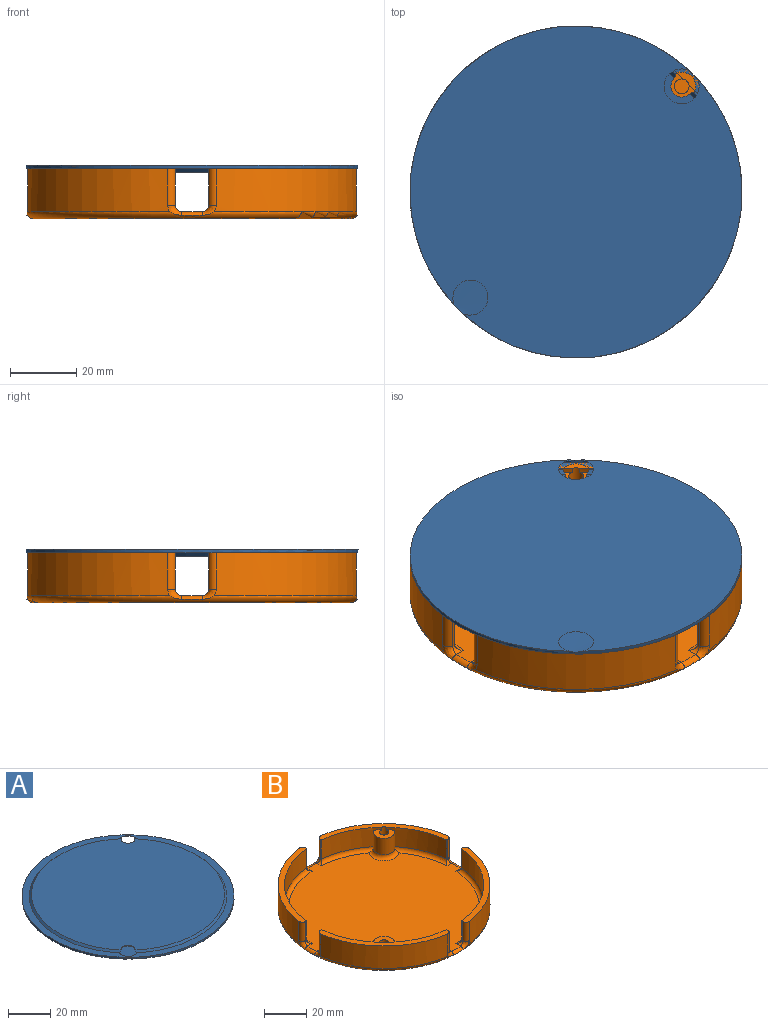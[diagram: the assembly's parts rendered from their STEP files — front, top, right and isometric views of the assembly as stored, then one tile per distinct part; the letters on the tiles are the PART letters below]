
ASSEMBLY  parts=2 mates=1
PART A: 8 faces, bbox 100x100x2 mm
  f0: cylinder r=50mm len=100mm, axis (0,0,-1), area 313mm2, adj f1,f2,f4,f5
  f1: plane 100x100mm, normal (0,0,1), area 1028.4mm2, adj f0,f4,f5,f6,f7
  f2: plane 100x100mm, normal (0,0,-1), area 7681.9mm2, adj f0,f4,f5
  f3: plane 91x91mm, normal (0,0,1), area 6464.7mm2, adj f4,f5,f6,f7
  f4: cone r=5.25mm half-angle=45deg, axis (0,0,-1), area 60.4mm2, adj f0,f1,f2,f3,f6,f7
  f5: cone r=5.25mm half-angle=45deg, axis (0,0,-1), area 60.4mm2, adj f0,f1,f2,f3,f6,f7
  f6: cone r=45.5mm half-angle=45deg, axis (0,0,-1), area 194.1mm2, adj f1,f3,f4,f5
  f7: cone r=45.5mm half-angle=45deg, axis (0,0,-1), area 194.1mm2, adj f1,f3,f4,f5
PART B: 69 faces, bbox 108.2x108.2x15 mm
  f0: cylinder r=5mm len=9.56mm, axis (0,0,-1), area 183.5mm2, adj f14,f16,f30,f68
  f1: cylinder r=5mm len=9.56mm, axis (0,0,-1), area 183.5mm2, adj f25,f27,f36,f67
  f2: cylinder r=50mm len=42.81mm, axis (0,0,-1), area 831.9mm2, adj f17,f42,f43,f55,f56,f64
  f3: cylinder r=50mm len=42.81mm, axis (0,0,-1), area 831.9mm2, adj f22,f46,f47,f58,f59,f64
  f4: cylinder r=50mm len=42.81mm, axis (0,0,-1), area 831.9mm2, adj f28,f50,f61,f64,f65,f66
  f5: plane 96x96mm, normal (0,0,1), area 6284.9mm2, adj f30,f31,f32,f33,f34,f35,f36,f37
  f6: cylinder r=50mm len=42.81mm, axis (0,0,-1), area 831.9mm2, adj f11,f38,f39,f52,f53,f64
  f7: plane 96x96mm, normal (0,0,-1), area 7238.2mm2, adj f64
  f8: plane 11x0.75mm, normal (1,0,0), area 8.3mm2, adj f10,f11,f37,f38
  f9: plane 11x0.75mm, normal (0,-1,0), area 8.3mm2, adj f10,f11,f39,f40
  f10: cylinder r=47mm len=41.73mm, axis (0,0,-1), area 701.9mm2, adj f8,f9,f11,f31
  f11: plane 44.49x44.49mm, normal (0,0,1), area 196.2mm2, adj f6,f8,f9,f10,f38,f39
  f12: plane 11x0.75mm, normal (0,1,0), area 8.3mm2, adj f16,f17,f41,f42
  f13: plane 11x0.75mm, normal (1,0,0), area 8.3mm2, adj f14,f17,f43,f44
  f14: cylinder r=47mm len=27.48mm, axis (0,0,-1), area 304.9mm2, adj f0,f13,f15,f17,f33,f68
  f15: cylinder r=2.25mm len=13mm, axis (0,0,-1), area 165.9mm2, adj f14,f16,f17,f18,f68
  f16: cylinder r=47mm len=27.48mm, axis (0,0,-1), area 304.9mm2, adj f0,f12,f15,f17,f32,f68
  f17: plane 44.49x44.49mm, normal (0,0,1), area 195.8mm2, adj f2,f12,f13,f14,f15,f16,f42,f43
  f18: plane 4.5x4.5mm, normal (0,0,1), area 15.9mm2, adj f15
  f19: plane 11x0.75mm, normal (0,1,0), area 8.3mm2, adj f20,f22,f47,f48
  f20: cylinder r=47mm len=41.73mm, axis (0,0,-1), area 701.9mm2, adj f19,f21,f22,f34
  f21: plane 11x0.75mm, normal (-1,0,0), area 8.3mm2, adj f20,f22,f45,f46
  f22: plane 44.49x44.49mm, normal (0,0,1), area 196.2mm2, adj f3,f19,f20,f21,f46,f47
  f23: plane 11x0.75mm, normal (0,-1,0), area 8.3mm2, adj f27,f28,f49,f50
  f24: plane 11x0.75mm, normal (-1,0,0), area 8.3mm2, adj f25,f28,f62,f66
  f25: cylinder r=47mm len=27.48mm, axis (0,0,-1), area 304.9mm2, adj f1,f24,f26,f28,f51,f67
  f26: cylinder r=2.25mm len=13mm, axis (0,0,-1), area 165.9mm2, adj f25,f27,f28,f29,f67
  f27: cylinder r=47mm len=27.48mm, axis (0,0,-1), area 304.9mm2, adj f1,f23,f26,f28,f35,f67
  f28: plane 44.49x44.49mm, normal (0,0,1), area 195.8mm2, adj f4,f23,f24,f25,f26,f27,f50,f66
  f29: plane 4.5x4.5mm, normal (0,0,1), area 15.9mm2, adj f26
  f30: torus R=7mm, axis (0,0,1), area 61.1mm2, adj f0,f5,f32,f33
  f31: torus R=45mm, axis (0,0,1), area 203.1mm2, adj f5,f10,f37,f40
  f32: torus R=45mm, axis (0,0,1), area 83mm2, adj f5,f16,f30,f41
  f33: torus R=45mm, axis (0,0,1), area 83mm2, adj f5,f14,f30,f44
  f34: torus R=45mm, axis (0,0,1), area 203.1mm2, adj f5,f20,f45,f48
  f35: torus R=45mm, axis (0,0,1), area 83mm2, adj f5,f27,f36,f49
  f36: torus R=7mm, axis (0,0,1), area 61.1mm2, adj f1,f5,f35,f51
  f37: cylinder r=2mm len=3.01mm, axis (0,1,0), area 5.9mm2, adj f5,f8,f31,f52
  f38: cylinder r=2mm len=11mm, axis (0,0,-1), area 37.8mm2, adj f6,f8,f11,f52
  f39: cylinder r=2mm len=11mm, axis (0,0,-1), area 37.8mm2, adj f6,f9,f11,f53
  f40: cylinder r=2mm len=3.01mm, axis (1,0,0), area 5.9mm2, adj f5,f9,f31,f53
  f41: cylinder r=2mm len=3.01mm, axis (-1,0,0), area 5.9mm2, adj f5,f12,f32,f55
  f42: cylinder r=2mm len=11mm, axis (0,0,-1), area 37.8mm2, adj f2,f12,f17,f55
  f43: cylinder r=2mm len=11mm, axis (0,0,-1), area 37.8mm2, adj f2,f13,f17,f56
  f44: cylinder r=2mm len=3.01mm, axis (0,1,0), area 5.9mm2, adj f5,f13,f33,f56
  f45: cylinder r=2mm len=3.01mm, axis (0,-1,0), area 5.9mm2, adj f5,f21,f34,f58
  f46: cylinder r=2mm len=11mm, axis (0,0,-1), area 37.8mm2, adj f3,f21,f22,f58
  f47: cylinder r=2mm len=11mm, axis (0,0,-1), area 37.8mm2, adj f3,f19,f22,f59
  f48: cylinder r=2mm len=3.01mm, axis (-1,0,0), area 5.9mm2, adj f5,f19,f34,f59
  f49: cylinder r=2mm len=3.01mm, axis (1,0,0), area 5.9mm2, adj f5,f23,f35,f61
  f50: cylinder r=2mm len=11mm, axis (0,0,-1), area 37.8mm2, adj f4,f23,f28,f61
  f51: torus R=45mm, axis (0,0,1), area 83mm2, adj f5,f25,f36,f62
  f52: bspline ~4.89x4.87mm, area 12.2mm2, adj f6,f37,f38,f63,f64
  f53: bspline ~5.1x4.7mm, area 12.2mm2, adj f6,f39,f40,f54,f64
  f54: torus R=48mm, axis (0,0,1), area 12.8mm2, adj f5,f53,f55,f64
  f55: bspline ~4.89x4.87mm, area 12.2mm2, adj f2,f41,f42,f54,f64
  f56: bspline ~5.1x4.7mm, area 12.2mm2, adj f2,f43,f44,f57,f64
  f57: torus R=48mm, axis (0,0,1), area 12.8mm2, adj f5,f56,f58,f64
  f58: bspline ~4.89x4.87mm, area 12.2mm2, adj f3,f45,f46,f57,f64
  f59: bspline ~5.1x4.7mm, area 12.2mm2, adj f3,f47,f48,f60,f64
  f60: torus R=48mm, axis (0,0,1), area 12.8mm2, adj f5,f59,f61,f64
  f61: bspline ~4.89x4.87mm, area 12.2mm2, adj f4,f49,f50,f60,f64
  f62: cylinder r=2mm len=3.01mm, axis (0,-1,0), area 5.9mm2, adj f5,f24,f51,f65
  f63: torus R=48mm, axis (0,0,1), area 12.8mm2, adj f5,f52,f64,f65
  f64: torus R=48mm, axis (0,0,1), area 931.3mm2, adj f2,f3,f4,f6,f7,f52,f53,f54
  f65: bspline ~5.1x4.7mm, area 12.2mm2, adj f4,f62,f63,f64,f66
  f66: cylinder r=2mm len=11mm, axis (0,0,-1), area 37.8mm2, adj f4,f24,f28,f65
  f67: plane 9.56x9.56mm, normal (0,0,1), area 42.5mm2, adj f1,f25,f26,f27
  f68: plane 9.56x9.56mm, normal (0,0,1), area 42.5mm2, adj f0,f14,f15,f16
PLACE A rot(axis=(0.71,0.71,0),180deg) t=(0,0,16)mm
PLACE B at identity fixed
MATE fastened A.f0 <-> B.f10  axis (0,0,-1) through (0,0,15)mm
